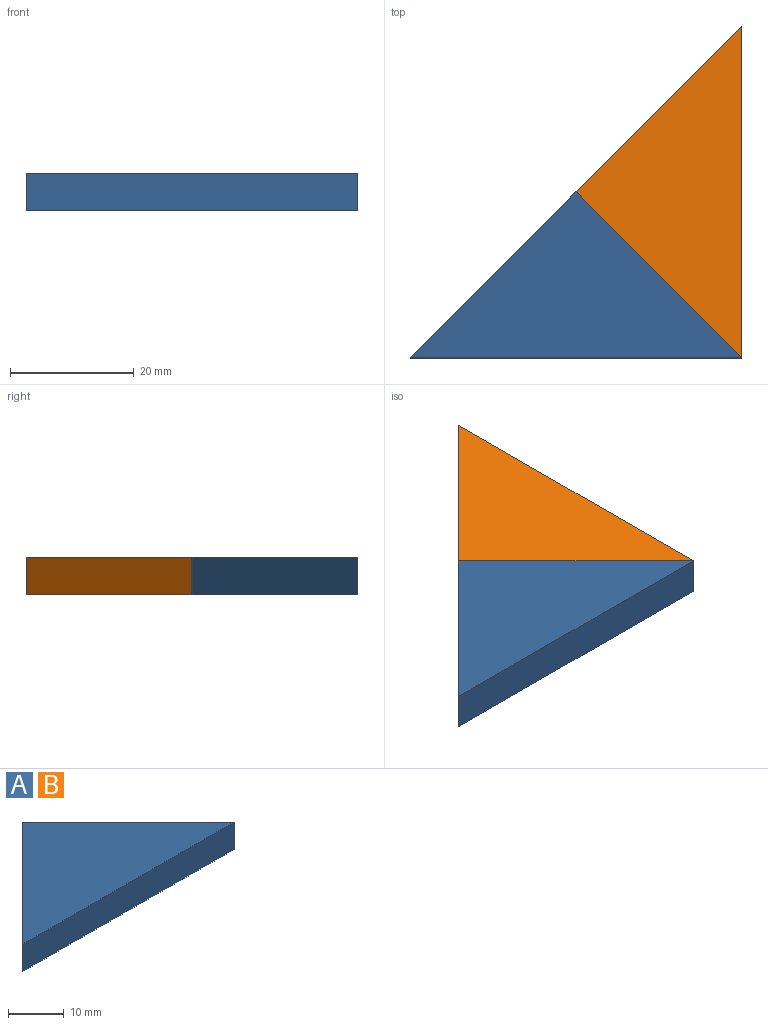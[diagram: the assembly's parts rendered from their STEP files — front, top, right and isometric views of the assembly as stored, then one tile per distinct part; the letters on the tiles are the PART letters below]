
ASSEMBLY  parts=2 mates=1
PART A: 5 faces, bbox 53.7x26.9x6 mm
  f0: plane 26.87x26.87mm, normal (-0.71,0.71,0), area 228mm2, adj f1,f2,f3,f4
  f1: plane 53.74x6mm, normal (0,-1,0), area 322.4mm2, adj f0,f2,f3,f4
  f2: plane 26.87x26.87mm, normal (0.71,0.71,0), area 228mm2, adj f0,f1,f3,f4
  f3: plane 53.74x26.87mm, normal (0,0,1), area 722mm2, adj f0,f1,f2
  f4: plane 53.74x26.87mm, normal (0,0,-1), area 722mm2, adj f0,f1,f2
PART B: same geometry as A
PLACE A t=(-3.8,-4.22,-9.16)mm
PLACE B rot(axis=(0.71,-0.71,0),180deg) t=(49.94,49.52,-3.16)mm
MATE fastened B.f2 <-> A.f2  axis (-0.71,-0.71,0) through (36.5,9.21,-6.16)mm
